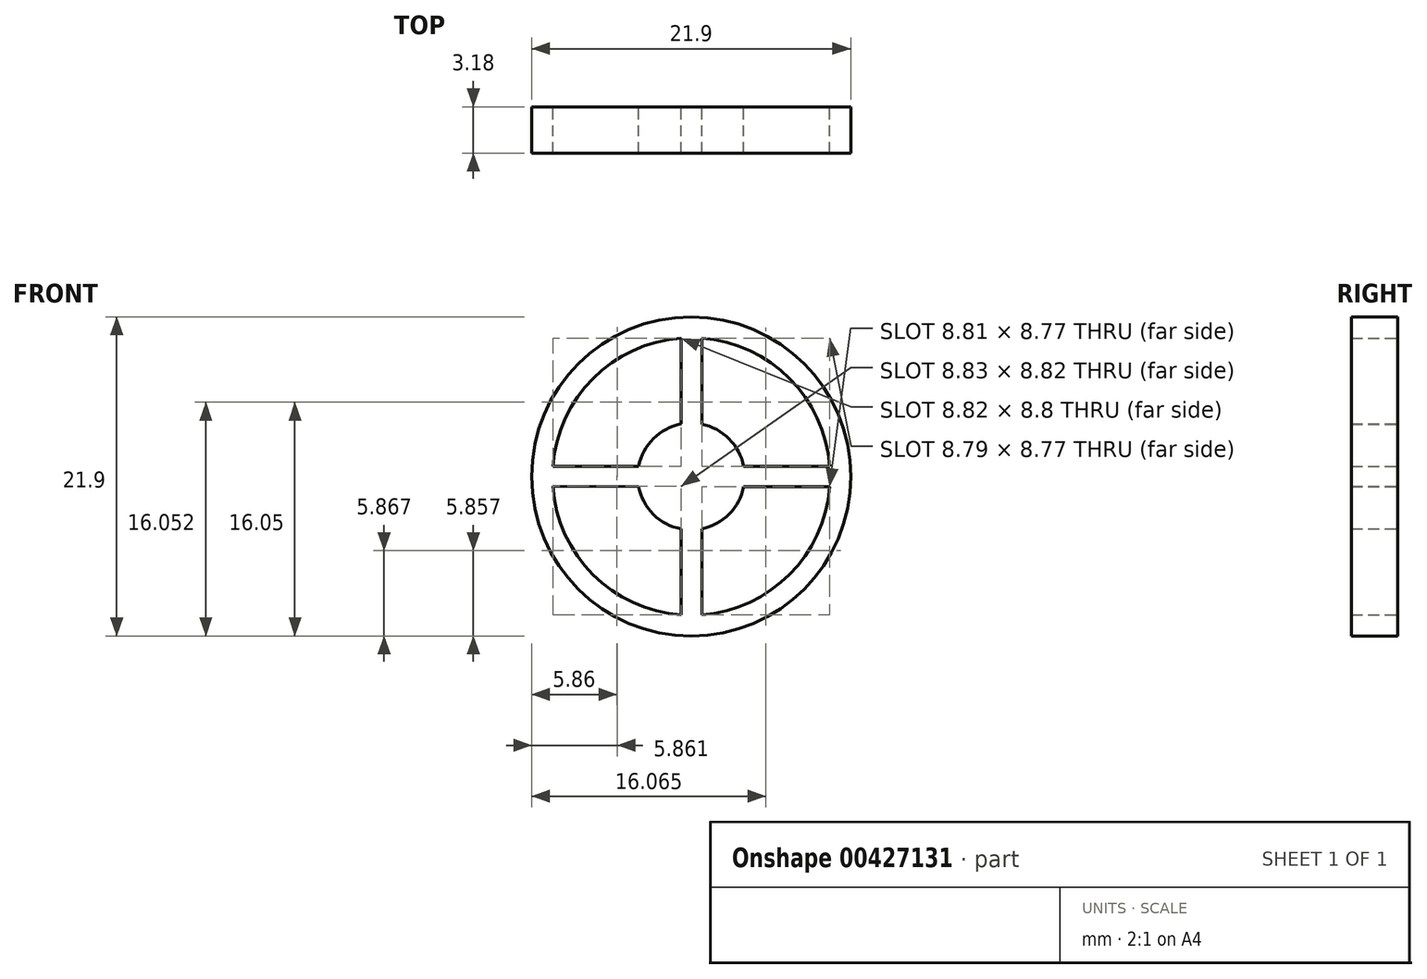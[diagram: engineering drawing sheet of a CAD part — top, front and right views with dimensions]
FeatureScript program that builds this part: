
annotation { "Feature Type Name" : "Feature", "Feature Type Description" : "" }
export const myFeature = defineFeature(function(context is Context, id is Id, definition is map)
    precondition{}
    {
        {
            var Q0;
            Q0=qCreatedBy(makeId("Front.planeOp"),FACE);
            var sketch = newSketch(context, id + "F0", { "sketchPlane" : qUnion([Q0])});
            skCircle(sketch, "E0", {"center": v(0, 0) * mm, "radius": 9.53 * mm});
            skCircle(sketch, "E1", {"center": v(0, 0) * mm, "radius": 3.67 * mm});
            skLineSegment(sketch, "E2", {"start": v(-3.6, 0.7) * mm, "end": v(-9.5, 0.7) * mm});
            skLineSegment(sketch, "E3", {"start": v(-9.5, -0.67) * mm, "end": v(-3.6, -0.69) * mm});
            skLineSegment(sketch, "E4", {"start": v(3.6, -0.69) * mm, "end": v(9.5, -0.71) * mm});
            skLineSegment(sketch, "E5", {"start": v(3.6, 0.7) * mm, "end": v(9.5, 0.7) * mm});
            skLineSegment(sketch, "E6", {"start": v(0.73, 9.5) * mm, "end": v(0.73, 3.6) * mm});
            skLineSegment(sketch, "E7", {"start": v(-0.68, -3.6) * mm, "end": v(-0.68, -9.5) * mm});
            skLineSegment(sketch, "E8", {"start": v(0.73, -3.6) * mm, "end": v(0.73, -9.5) * mm});
            skCircle(sketch, "E9", {"center": v(0, 0) * mm, "radius": 10.95 * mm});
            skLineSegment(sketch, "E10", {"start": v(-0.68, 3.6) * mm, "end": v(-0.68, 9.5) * mm});
            skSolve(sketch);
        }
        {
            var Q0;
            Q0=makeQuery(id+"F0.imprint","IMPRINT",FACE,{"disambiguationData":[TD([[makeQuery(id+"F0.imprint","IMPRINT",EDGE,{"derivedFrom":sQuery(id+"F0.wireOp",EDGE,"E9")}),1.0]])]});
            var Q1;
            {var subQ0=sQuery(id+"F0.wireOp",EDGE,"E1");var subQ5=makeQuery(id+"F0.imprint","INTERSECT",VERTEX,{"derivedFrom":[subQ0,sQuery(id+"F0.wireOp",EDGE,"E5")]});Q1=makeQuery(id+"F0.imprint","IMPRINT",FACE,{"disambiguationData":[TD([[makeQuery(id+"F0.imprint","IMPRINT",EDGE,{"disambiguationData":[TD([[subQ5,-1.0]])],"derivedFrom":subQ0}),1.0]])]});}
            var Q2;
            {var subQ0=sQuery(id+"F0.wireOp",EDGE,"E7");Q2=makeQuery(id+"F0.imprint","IMPRINT",FACE,{"disambiguationData":[TD([[makeQuery(id+"F0.imprint","IMPRINT",EDGE,{"derivedFrom":subQ0}),1.0]])]});}
            var Q3;
            {var subQ0=sQuery(id+"F0.wireOp",EDGE,"E2");Q3=makeQuery(id+"F0.imprint","IMPRINT",FACE,{"disambiguationData":[TD([[makeQuery(id+"F0.imprint","IMPRINT",EDGE,{"derivedFrom":subQ0}),1.0]])]});}
            var Q4;
            {var subQ0=sQuery(id+"F0.wireOp",EDGE,"E4");Q4=makeQuery(id+"F0.imprint","IMPRINT",FACE,{"disambiguationData":[TD([[makeQuery(id+"F0.imprint","IMPRINT",EDGE,{"derivedFrom":subQ0}),1.0]])]});}
            var Q5;
            {var subQ0=sQuery(id+"F0.wireOp",EDGE,"E6");Q5=makeQuery(id+"F0.imprint","IMPRINT",FACE,{"disambiguationData":[TD([[makeQuery(id+"F0.imprint","IMPRINT",EDGE,{"derivedFrom":subQ0}),-1.0]])]});}
            extrude(context, id + "F1", {"entities" : qUnion([Q0, Q1, Q2, Q3, Q4, Q5]), "depth" : 3.17 * mm});
        }
    });
